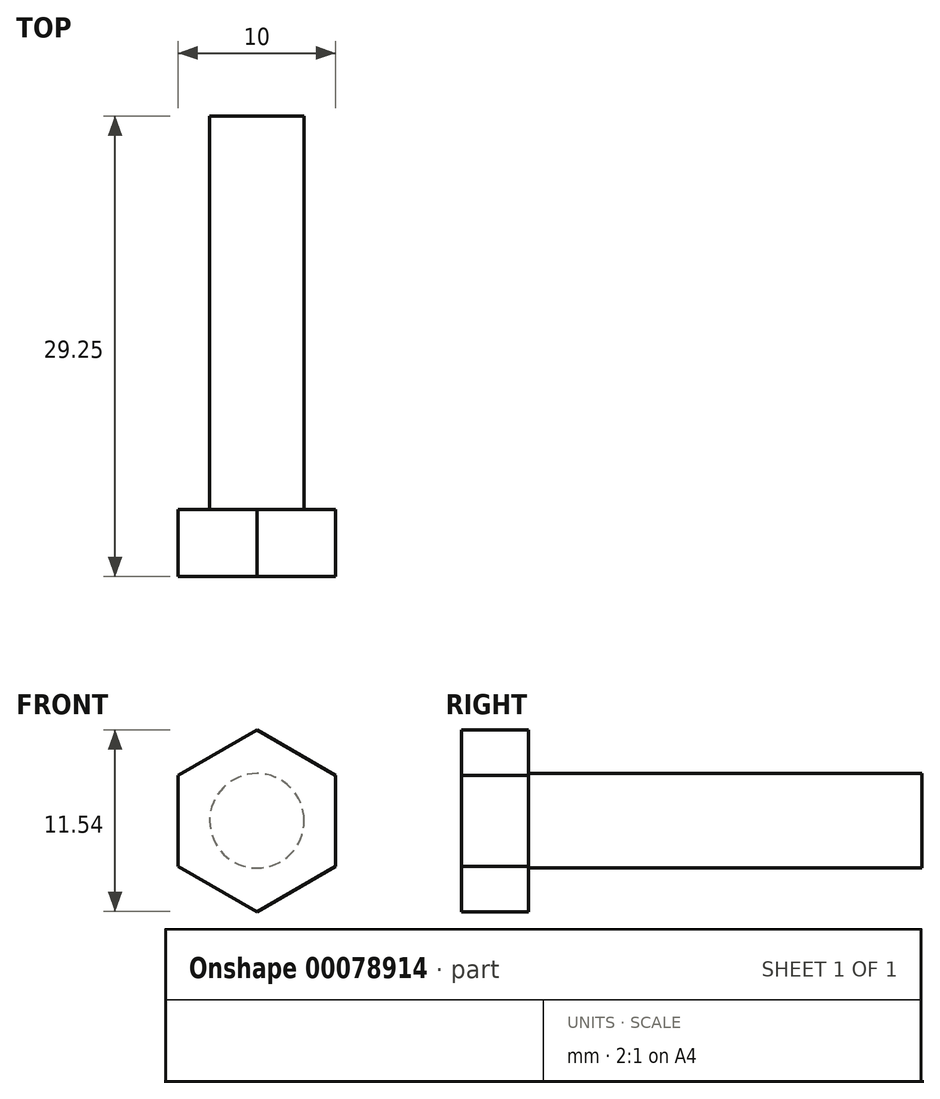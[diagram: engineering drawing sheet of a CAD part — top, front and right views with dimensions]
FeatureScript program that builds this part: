
annotation { "Feature Type Name" : "Feature", "Feature Type Description" : "" }
export const myFeature = defineFeature(function(context is Context, id is Id, definition is map)
    precondition{}
    {
        {
            var Q0;
            Q0=qCreatedBy(makeId("Front.planeOp"),FACE);
            var sketch = newSketch(context, id + "F0", { "sketchPlane" : qUnion([Q0])});
            skCircle(sketch, "E0", {"center": v(0, 0) * mm, "radius": 3 * mm});
            skCircle(sketch, "E1.cCircle", {"center": v(0, 0) * mm, "radius": 5 * mm, "construction": true});
            skLineSegment(sketch, "E1.0", {"start": v(5, 2.89) * mm, "end": v(5, -2.89) * mm});
            skLineSegment(sketch, "E1.1", {"start": v(5, -2.89) * mm, "end": v(0, -5.77) * mm});
            skLineSegment(sketch, "E1.2", {"start": v(0, -5.77) * mm, "end": v(-5, -2.89) * mm});
            skLineSegment(sketch, "E1.3", {"start": v(-5, -2.89) * mm, "end": v(-5, 2.89) * mm});
            skLineSegment(sketch, "E1.4", {"start": v(-5, 2.89) * mm, "end": v(0, 5.77) * mm});
            skLineSegment(sketch, "E1.5", {"start": v(0, 5.77) * mm, "end": v(5, 2.89) * mm});
            skPoint(sketch, "E1.0.midPoint", {"position": v(5, 0) * mm});
            skSolve(sketch);
        }
        {
            var Q0;
            Q0=makeQuery(id+"F0.imprint","IMPRINT",FACE,{"disambiguationData":[TD([[makeQuery(id+"F0.imprint","IMPRINT",EDGE,{"derivedFrom":sQuery(id+"F0.wireOp",EDGE,"E0")}),-1.0]])]});
            var Q1;
            Q1=makeQuery(id+"F0.imprint","IMPRINT",FACE,{"disambiguationData":[TD([[makeQuery(id+"F0.imprint","IMPRINT",EDGE,{"derivedFrom":sQuery(id+"F0.wireOp",EDGE,"E0")}),1.0]])]});
            extrude(context, id + "F1", {"entities" : qUnion([Q0, Q1]), "depth" : 4.25 * mm});
        }
        {
            var Q0;
            Q0=makeQuery(id+"F0.imprint","IMPRINT",FACE,{"disambiguationData":[TD([[makeQuery(id+"F0.imprint","IMPRINT",EDGE,{"derivedFrom":sQuery(id+"F0.wireOp",EDGE,"E0")}),1.0]])]});
            extrude(context, id + "F2", {"entities" : qUnion([Q0]), "operationType" : NewBodyOperationType.ADD, "oppositeDirection" : true, "depth" : 25 * mm});
        }
    });
